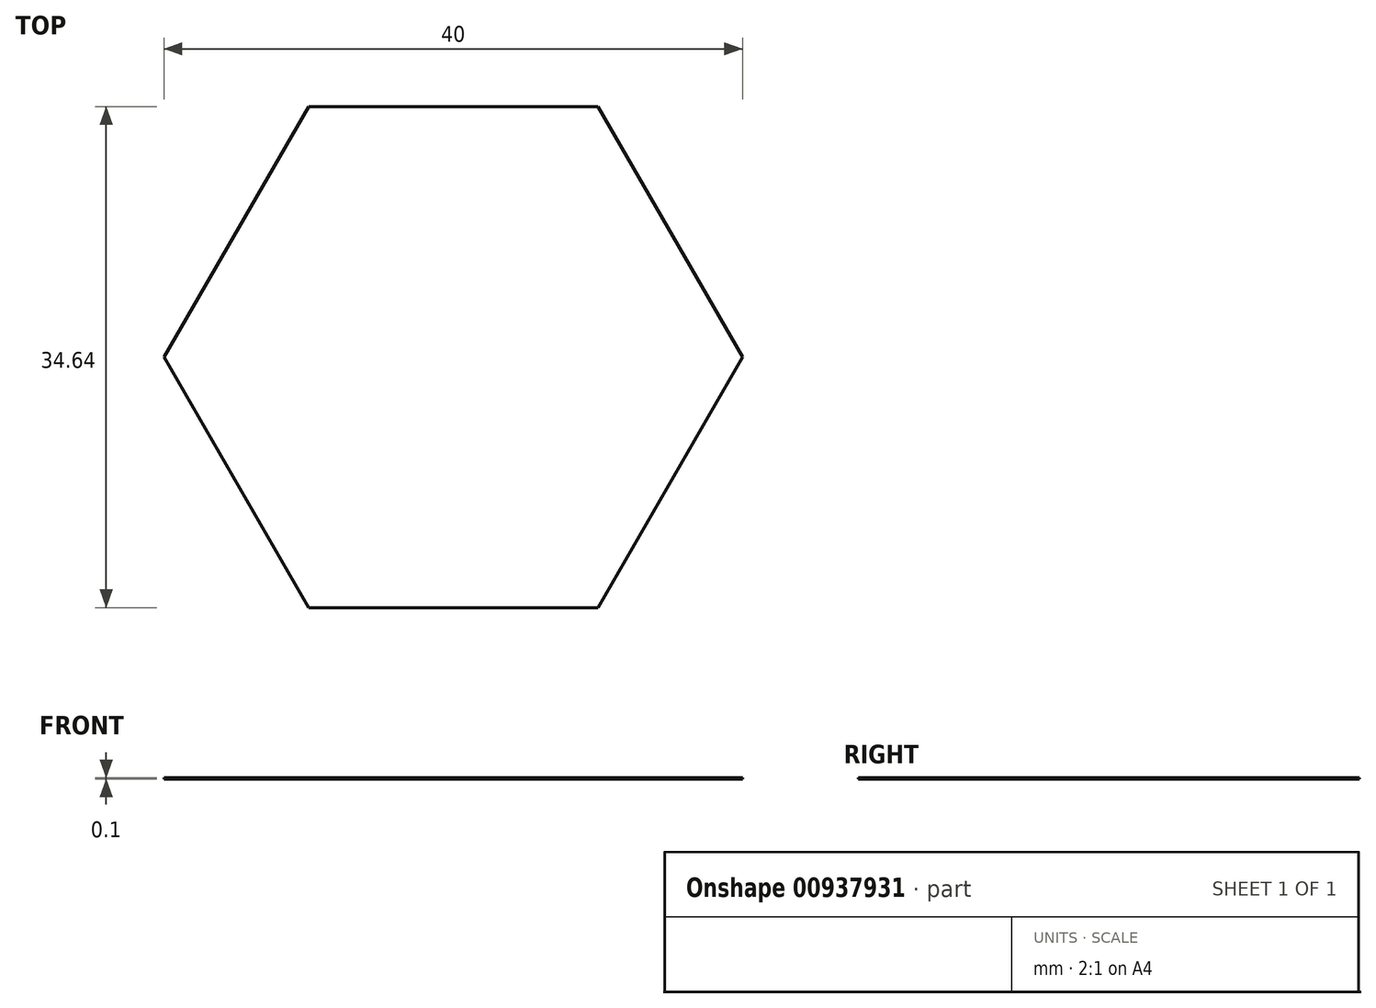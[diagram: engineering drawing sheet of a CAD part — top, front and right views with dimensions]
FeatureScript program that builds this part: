
annotation { "Feature Type Name" : "Feature", "Feature Type Description" : "" }
export const myFeature = defineFeature(function(context is Context, id is Id, definition is map)
    precondition{}
    {
        {
            var Q0;
            Q0=qCreatedBy(makeId("Top.planeOp"),FACE);
            var sketch = newSketch(context, id + "F0", { "sketchPlane" : qUnion([Q0])});
            skCircle(sketch, "E0.cCircle", {"center": v(0, 0) * mm, "radius": 17.32 * mm, "construction": true});
            skLineSegment(sketch, "E0.0", {"start": v(20, 0) * mm, "end": v(10, -17.32) * mm});
            skLineSegment(sketch, "E0.1", {"start": v(10, -17.32) * mm, "end": v(-10, -17.32) * mm});
            skLineSegment(sketch, "E0.2", {"start": v(-10, -17.32) * mm, "end": v(-20, 0) * mm});
            skLineSegment(sketch, "E0.3", {"start": v(-20, 0) * mm, "end": v(-10, 17.32) * mm});
            skLineSegment(sketch, "E0.4", {"start": v(-10, 17.32) * mm, "end": v(10, 17.32) * mm});
            skLineSegment(sketch, "E0.5", {"start": v(10, 17.32) * mm, "end": v(20, 0) * mm});
            skPoint(sketch, "E0.0.midPoint", {"position": v(15, -8.66) * mm});
            skLineSegment(sketch, "E1", {"start": v(0, 0) * mm, "end": v(0, 21.66) * mm, "construction": true});
            skSolve(sketch);
        }
        {
            var Q0;
            Q0=qSketchRegion(id+"F0",true);
            extrude(context, id + "F1", {"entities" : qUnion([Q0]), "depth" : 0.1 * mm, "offsetDistance" : 25 * mm});
        }
    });
